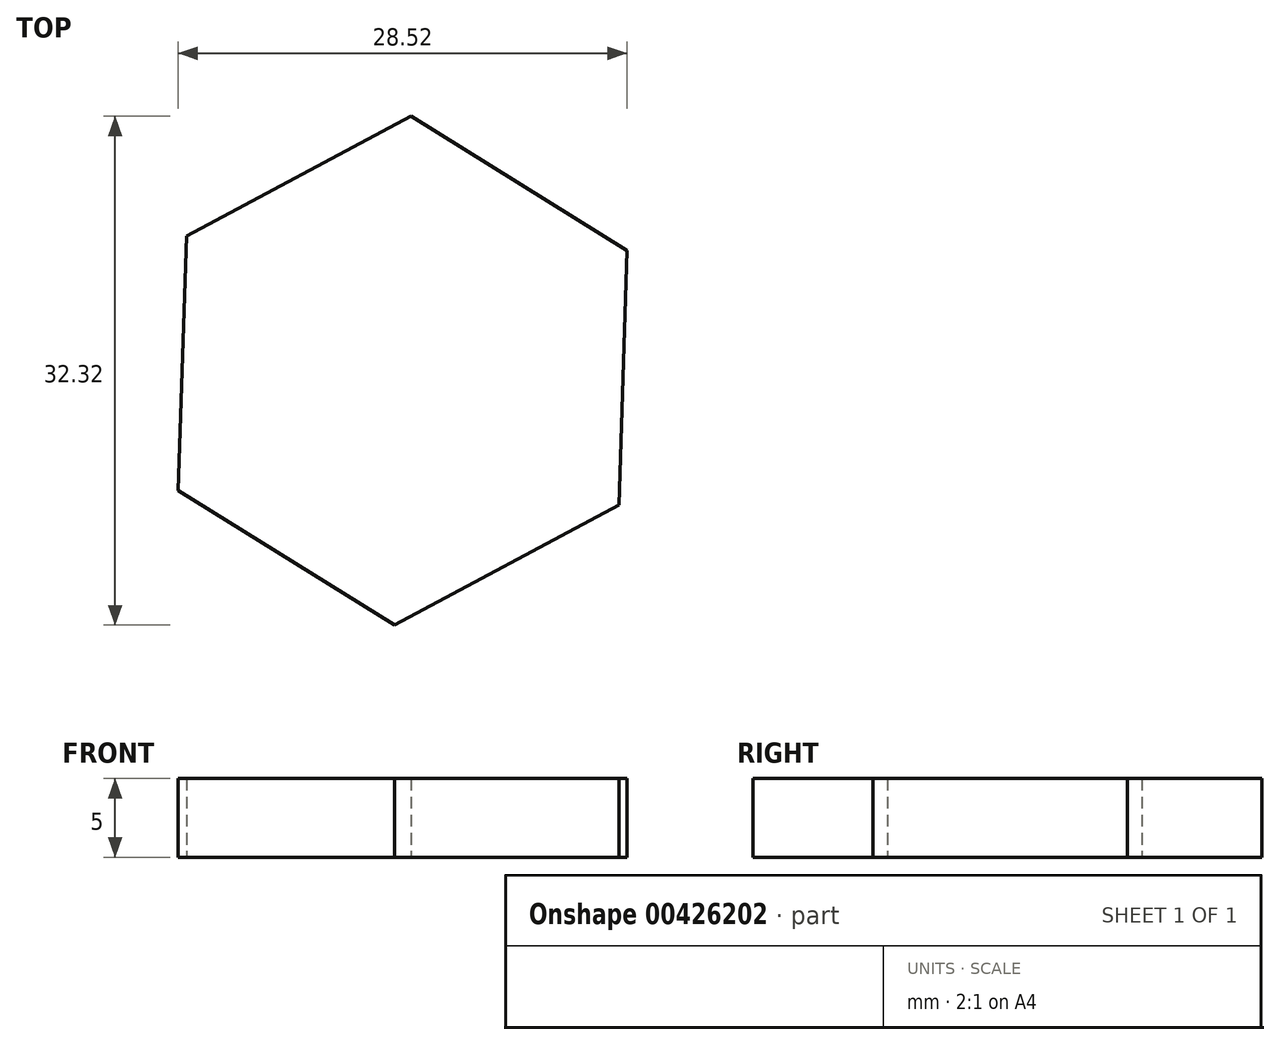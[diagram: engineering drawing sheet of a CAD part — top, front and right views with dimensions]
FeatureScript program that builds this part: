
annotation { "Feature Type Name" : "Feature", "Feature Type Description" : "" }
export const myFeature = defineFeature(function(context is Context, id is Id, definition is map)
    precondition{}
    {
        {
            var Q0;
            Q0=qCreatedBy(makeId("Top.planeOp"),FACE);
            var sketch = newSketch(context, id + "F0", { "sketchPlane" : qUnion([Q0])});
            skCircle(sketch, "E0.cCircle", {"center": v(0, 0) * mm, "radius": 14 * mm, "construction": true});
            skLineSegment(sketch, "E0.0", {"start": v(0.53, 16.16) * mm, "end": v(14.26, 7.62) * mm});
            skLineSegment(sketch, "E0.1", {"start": v(14.26, 7.62) * mm, "end": v(13.73, -8.54) * mm});
            skLineSegment(sketch, "E0.2", {"start": v(13.73, -8.54) * mm, "end": v(-0.53, -16.16) * mm});
            skLineSegment(sketch, "E0.3", {"start": v(-0.53, -16.16) * mm, "end": v(-14.26, -7.62) * mm});
            skLineSegment(sketch, "E0.4", {"start": v(-14.26, -7.62) * mm, "end": v(-13.73, 8.54) * mm});
            skLineSegment(sketch, "E0.5", {"start": v(-13.73, 8.54) * mm, "end": v(0.53, 16.16) * mm});
            skPoint(sketch, "E0.0.midPoint", {"position": v(7.4, 11.89) * mm});
            skSolve(sketch);
        }
        {
            var Q0;
            Q0 = qSketchRegion(id + "F0", true);
            extrude(context, id + "F1", {"entities" : qUnion([Q0]), "depth" : 5 * mm});
        }
    });
